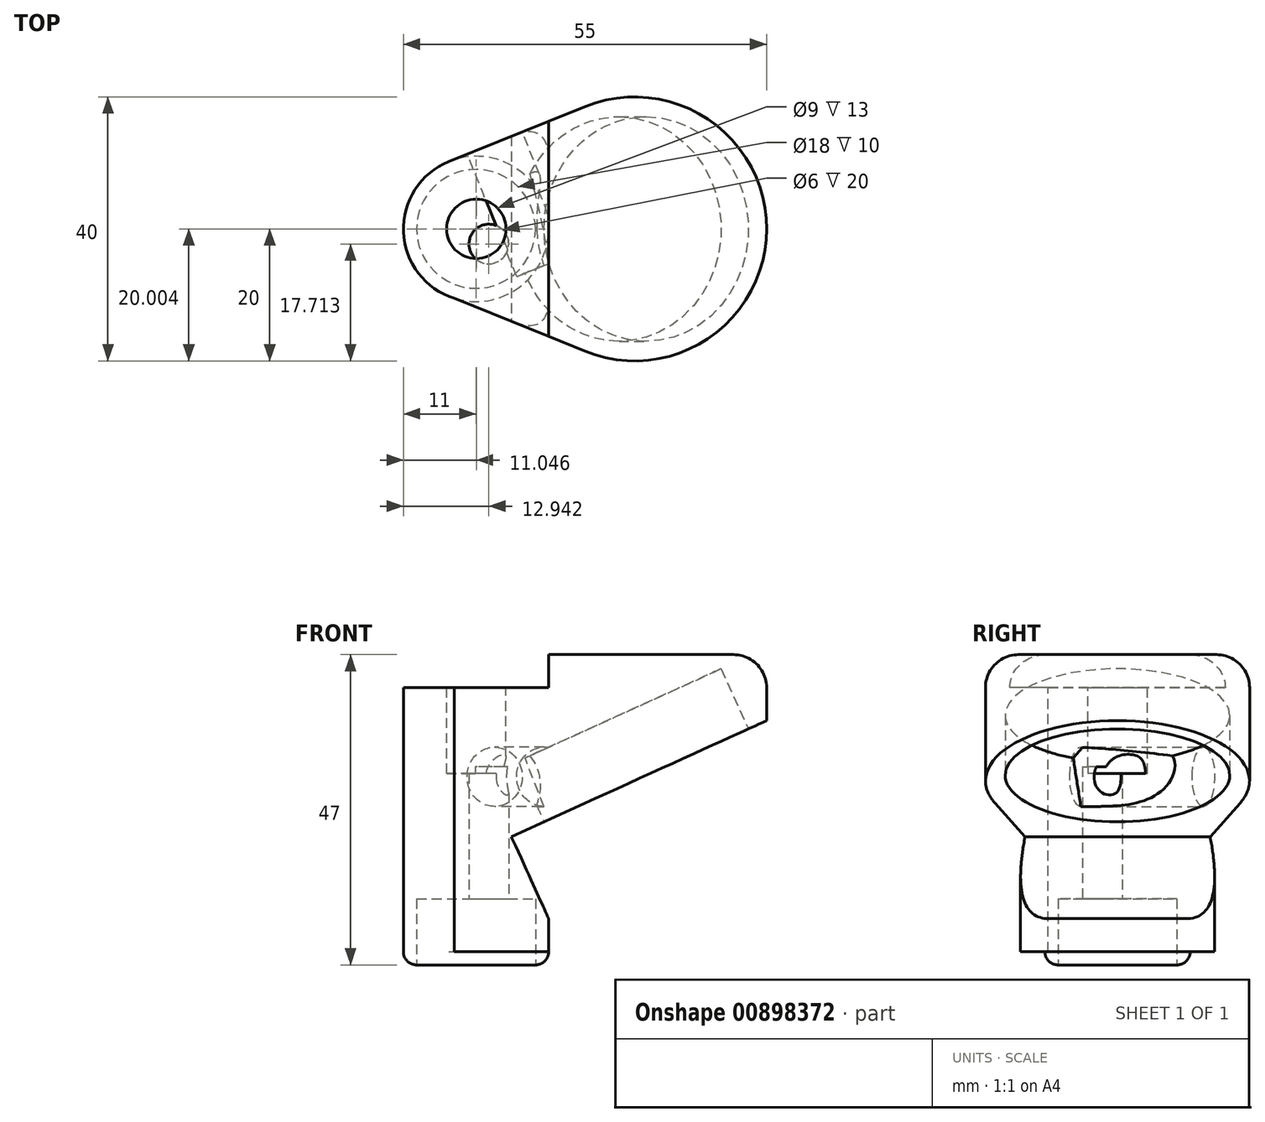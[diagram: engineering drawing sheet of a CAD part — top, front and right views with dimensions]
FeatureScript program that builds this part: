
annotation { "Feature Type Name" : "Feature", "Feature Type Description" : "" }
export const myFeature = defineFeature(function(context is Context, id is Id, definition is map)
    precondition{}
    {
        {
            var Q0;
            Q0=qCreatedBy(makeId("Top.planeOp"),FACE);
            var sketch = newSketch(context, id + "F0", { "sketchPlane" : qUnion([Q0])});
            skLineSegment(sketch, "E0.bottom", {"start": v(27.5, -20) * mm, "end": v(-27.5, -20) * mm});
            skLineSegment(sketch, "E0.top", {"start": v(27.5, 20) * mm, "end": v(-27.5, 20) * mm});
            skLineSegment(sketch, "E0.left", {"start": v(27.5, -20) * mm, "end": v(27.5, 20) * mm});
            skLineSegment(sketch, "E0.right", {"start": v(-27.5, -20) * mm, "end": v(-27.5, 20) * mm});
            skPoint(sketch, "E0.middle", {"position": v(0, 0) * mm});
            skSolve(sketch);
        }
        {
            var Q0;
            Q0=makeQuery(id+"F0.imprint","IMPRINT",FACE,{"disambiguationData":[TD([[makeQuery(id+"F0.imprint","IMPRINT",EDGE,{"derivedFrom":sQuery(id+"F0.wireOp",EDGE,"E0.bottom")}),-1.0]])]});
            extrude(context, id + "F1", {"entities" : qUnion([Q0]), "depth" : 45 * mm, "offsetDistance" : 25 * mm});
        }
        {
            var Q0;
            Q0=makeQuery(id+"F1.opExtrude","CAP_FACE",FACE,{"disambiguationData":[OSD([sQuery(id+"F0.wireOp",EDGE,"E0.bottom"),sQuery(id+"F0.wireOp",EDGE,"E0.top"),sQuery(id+"F0.wireOp",EDGE,"E0.left"),sQuery(id+"F0.wireOp",EDGE,"E0.right")])],"isStart":false});
            var sketch = newSketch(context, id + "F2", { "sketchPlane" : qUnion([Q0])});
            skPoint(sketch, "E1.first.point", {"position": v(27.5, 0) * mm});
            skLineSegment(sketch, "E2", {"start": v(6.08, -20) * mm, "end": v(27.5, -20) * mm});
            skLineSegment(sketch, "E3", {"start": v(27.5, 20) * mm, "end": v(6.08, 20) * mm});
            skCircle(sketch, "E4", {"center": v(-16.5, 0) * mm, "radius": 11 * mm});
            skPoint(sketch, "E4.centerSnap0", {"position": v(-16.5, 20) * mm});
            skLineSegment(sketch, "E5.left", {"start": v(27.5, 20) * mm, "end": v(27.5, -20) * mm});
            skCircle(sketch, "E6", {"center": v(7.5, 0) * mm, "radius": 20 * mm});
            skPoint(sketch, "E6.centerSnap0", {"position": v(7.5, 20) * mm});
            skLineSegment(sketch, "E7", {"start": v(-20.63, 10.2) * mm, "end": v(0, 18.54) * mm});
            skLineSegment(sketch, "E8", {"start": v(-19.77, -10.5) * mm, "end": v(0, -18.54) * mm});
            skSolve(sketch);
        }
        {
            var Q0;
            Q0=makeQuery(id+"F1.opExtrude","SWEPT_FACE",FACE,{"disambiguationData":[OSD([sQuery(id+"F0.wireOp",EDGE,"E0.bottom")])]});
            var sketch = newSketch(context, id + "F3", { "sketchPlane" : qUnion([Q0])});
            skLineSegment(sketch, "E9.bottom", {"start": v(27.5, 0) * mm, "end": v(-5.5, 0) * mm});
            skLineSegment(sketch, "E9.top", {"start": v(27.5, 5) * mm, "end": v(-5.5, 5) * mm});
            skLineSegment(sketch, "E9.left", {"start": v(27.5, 0) * mm, "end": v(27.5, 5) * mm});
            skLineSegment(sketch, "E9.right", {"start": v(-5.5, 0) * mm, "end": v(-5.5, 5) * mm});
            skLineSegment(sketch, "E10", {"start": v(27.5, 5) * mm, "end": v(27.5, 35) * mm});
            skLineSegment(sketch, "E11", {"start": v(27.5, 35) * mm, "end": v(-5.5, 20) * mm});
            skLineSegment(sketch, "E12", {"start": v(-5.5, 20) * mm, "end": v(-11.15, 17.43) * mm});
            skLineSegment(sketch, "E13", {"start": v(-11.15, 17.43) * mm, "end": v(-5.5, 5) * mm});
            skSolve(sketch);
        }
        {
            var Q0;
            Q0 = qSketchRegion(id + "F3", true);
            extrude(context, id + "F4", {"entities" : qUnion([Q0]), "operationType" : NewBodyOperationType.REMOVE, "endBound" : BoundingType.THROUGH_ALL, "oppositeDirection" : true, "depth" : 25 * mm, "offsetDistance" : 25 * mm});
        }
        {
            var Q0;
            Q0=makeQuery(id+"F1.opExtrude","CAP_FACE",FACE,{"disambiguationData":[OSD([sQuery(id+"F0.wireOp",EDGE,"E0.bottom"),sQuery(id+"F0.wireOp",EDGE,"E0.top"),sQuery(id+"F0.wireOp",EDGE,"E0.left"),sQuery(id+"F0.wireOp",EDGE,"E0.right")])],"isStart":true});
            var sketch = newSketch(context, id + "F5", { "sketchPlane" : qUnion([Q0])});
            skCircle(sketch, "E14", {"center": v(-16.5, 0) * mm, "radius": 11 * mm});
            skPoint(sketch, "E14.centerSnap0", {"position": v(-16.5, -20) * mm});
            skSolve(sketch);
        }
        {
            var Q0;
            {var subQ0=sQuery(id+"F5.wireOp",EDGE,"E14");var subQ1=makeQuery(id+"F5.imprint","INTERSECT",VERTEX,{"derivedFrom":[makeQuery(id+"F1.opExtrude","CAP_EDGE",EDGE,{"disambiguationData":[OSD([sQuery(id+"F0.wireOp",EDGE,"E0.right")])],"isStart":true}),subQ0]});Q0=makeQuery(id+"F5.imprint","IMPRINT",FACE,{"disambiguationData":[TD([[makeQuery(id+"F5.imprint","IMPRINT",EDGE,{"disambiguationData":[TD([[subQ1,1.0]])],"derivedFrom":subQ0}),1.0]])]});}
            extrude(context, id + "F6", {"entities" : qUnion([Q0]), "operationType" : NewBodyOperationType.ADD, "depth" : 2 * mm, "offsetDistance" : 25 * mm});
        }
        {
            var Q0;
            Q0=makeQuery(id+"F6.opExtrude","CAP_FACE",FACE,{"disambiguationData":[OSD([sQuery(id+"F5.wireOp",EDGE,"E14")])],"isStart":false});
            fillet(context, id + "F7", {"entities" : qUnion([Q0]), "radius" : 2 * mm, "tangentPropagation" : true, "allowEdgeOverflow" : false});
        }
        {
            var Q0;
            Q0=makeQuery(id+"F1.opExtrude","SWEPT_FACE",FACE,{"disambiguationData":[OSD([sQuery(id+"F0.wireOp",EDGE,"E0.bottom")])]});
            var sketch = newSketch(context, id + "F8", { "sketchPlane" : qUnion([Q0])});
            skLineSegment(sketch, "E15.bottom", {"start": v(-27.5, 45) * mm, "end": v(-5.5, 45) * mm});
            skLineSegment(sketch, "E15.top", {"start": v(-27.5, 40) * mm, "end": v(-5.5, 40) * mm});
            skLineSegment(sketch, "E15.left", {"start": v(-27.5, 45) * mm, "end": v(-27.5, 40) * mm});
            skLineSegment(sketch, "E15.right", {"start": v(-5.5, 45) * mm, "end": v(-5.5, 40) * mm});
            skSolve(sketch);
        }
        {
            var Q0;
            {var subQ4=sQuery(id+"F2.wireOp",EDGE,"E8");Q0=makeQuery(id+"F2.imprint","IMPRINT",FACE,{"disambiguationData":[TD([[makeQuery(id+"F2.imprint","IMPRINT",EDGE,{"derivedFrom":subQ4}),-1.0]])]});}
            var Q1;
            {var subQ4=sQuery(id+"F2.wireOp",EDGE,"E7");Q1=makeQuery(id+"F2.imprint","IMPRINT",FACE,{"disambiguationData":[TD([[makeQuery(id+"F2.imprint","IMPRINT",EDGE,{"derivedFrom":subQ4}),1.0]])]});}
            extrude(context, id + "F9", {"entities" : qUnion([Q0, Q1]), "operationType" : NewBodyOperationType.REMOVE, "endBound" : BoundingType.THROUGH_ALL, "oppositeDirection" : true, "depth" : 25 * mm, "offsetDistance" : 25 * mm});
        }
        {
            var Q0;
            Q0=makeQuery(id+"F8.imprint","IMPRINT",FACE,{"disambiguationData":[TD([[makeQuery(id+"F8.imprint","IMPRINT",EDGE,{"derivedFrom":sQuery(id+"F8.wireOp",EDGE,"E15.bottom")}),1.0]])]});
            extrude(context, id + "F10", {"entities" : qUnion([Q0]), "operationType" : NewBodyOperationType.REMOVE, "endBound" : BoundingType.THROUGH_ALL, "oppositeDirection" : true, "depth" : 25 * mm, "offsetDistance" : 25 * mm});
        }
        {
            var Q0;
            Q0=makeQuery(id+"F10.boolean.opBoolean","COPY",FACE,{"derivedFrom":makeQuery(id+"F10.opExtrude","SWEPT_FACE",FACE,{"disambiguationData":[OSD([sQuery(id+"F8.wireOp",EDGE,"E15.top")])]})});
            var sketch = newSketch(context, id + "F11", { "sketchPlane" : qUnion([Q0])});
            skCircle(sketch, "E16", {"center": v(-16.45, 0) * mm, "radius": 4.5 * mm});
            skSolve(sketch);
        }
        {
            var Q0;
            Q0=makeQuery(id+"F11.imprint","IMPRINT",FACE,{"disambiguationData":[TD([[makeQuery(id+"F11.imprint","IMPRINT",EDGE,{"derivedFrom":sQuery(id+"F11.wireOp",EDGE,"E16")}),1.0]])]});
            extrude(context, id + "F12", {"entities" : qUnion([Q0]), "operationType" : NewBodyOperationType.REMOVE, "oppositeDirection" : true, "depth" : 13 * mm, "offsetDistance" : 25 * mm});
        }
        {
            var Q0;
            Q0=makeQuery(id+"F4.boolean.opBoolean","COPY",FACE,{"derivedFrom":makeQuery(id+"F4.opExtrude","SWEPT_FACE",FACE,{"disambiguationData":[OSD([sQuery(id+"F3.wireOp",EDGE,"E11"),sQuery(id+"F3.wireOp",EDGE,"E12")])]})});
            var sketch = newSketch(context, id + "F13", { "sketchPlane" : qUnion([Q0])});
            skPoint(sketch, "E17.first.point", {"position": v(39.52, 0) * mm});
            skPoint(sketch, "E17.second.point", {"position": v(20.48, 20) * mm});
            skPoint(sketch, "E17.third.point", {"position": v(19.91, -20) * mm});
            skCircle(sketch, "E18", {"center": v(19.5, 0) * mm, "radius": 17 * mm});
            skSolve(sketch);
        }
        {
            var Q0;
            Q0=makeQuery(id+"F13.imprint","IMPRINT",FACE,{"disambiguationData":[TD([[makeQuery(id+"F13.imprint","IMPRINT",EDGE,{"derivedFrom":sQuery(id+"F13.wireOp",EDGE,"E18")}),1.0]])]});
            extrude(context, id + "F14", {"entities" : qUnion([Q0]), "operationType" : NewBodyOperationType.REMOVE, "oppositeDirection" : true, "depth" : 10 * mm, "offsetDistance" : 25 * mm});
        }
        {
            var Q0;
            Q0=makeQuery(id+"F6.opExtrude","CAP_FACE",FACE,{"disambiguationData":[OSD([sQuery(id+"F5.wireOp",EDGE,"E14")])],"isStart":false});
            extrude(context, id + "F15", {"entities" : qUnion([Q0]), "operationType" : NewBodyOperationType.REMOVE, "oppositeDirection" : true, "depth" : 10 * mm, "offsetDistance" : 25 * mm});
        }
        {
            var Q0;
            {var subQ0=sQuery(id+"F2.wireOp",EDGE,"E5.left");var subQ1=sQuery(id+"F2.wireOp",EDGE,"E2");var subQ2=makeQuery(id+"F2.imprint","INTERSECT",VERTEX,{"derivedFrom":[subQ1,subQ0]});Q0=makeQuery(id+"F2.imprint","IMPRINT",FACE,{"disambiguationData":[TD([[makeQuery(id+"F2.imprint","IMPRINT",EDGE,{"disambiguationData":[TD([[subQ2,-1.0]])],"derivedFrom":subQ1}),-1.0]])]});}
            extrude(context, id + "F16", {"entities" : qUnion([Q0]), "operationType" : NewBodyOperationType.REMOVE, "endBound" : BoundingType.THROUGH_ALL, "oppositeDirection" : true, "depth" : 25 * mm, "offsetDistance" : 25 * mm});
        }
        {
            var Q0;
            Q0=makeQuery(id+"F1.opExtrude","SWEPT_EDGE",EDGE,{"disambiguationData":[OSD([sQuery(id+"F0.wireOp",EDGE,"E0.top"),sQuery(id+"F0.wireOp",EDGE,"E0.left")])]});
            fillet(context, id + "F17", {"entities" : qUnion([Q0]), "radius" : 20 * mm, "tangentPropagation" : true, "allowEdgeOverflow" : false});
        }
        {
            var Q0;
            Q0=makeQuery(id+"F9.boolean.opBoolean","INTERSECT",EDGE,{"derivedFrom":[makeQuery(id+"F4.boolean.opBoolean","COPY",FACE,{"derivedFrom":makeQuery(id+"F4.opExtrude","SWEPT_FACE",FACE,{"disambiguationData":[OSD([sQuery(id+"F3.wireOp",EDGE,"E9.right")])]})}),makeQuery(id+"F9.opExtrude","SWEPT_FACE",FACE,{"disambiguationData":[OSD([sQuery(id+"F2.wireOp",EDGE,"E7")])]})]});
            fillet(context, id + "F18", {"entities" : qUnion([Q0]), "radius" : 4 * mm, "tangentPropagation" : true, "rho" : 0.5, "crossSection" : FilletCrossSection.CONIC, "allowEdgeOverflow" : false});
        }
        {
            var Q0;
            Q0=makeQuery(id+"F9.boolean.opBoolean","INTERSECT",EDGE,{"derivedFrom":[makeQuery(id+"F4.boolean.opBoolean","COPY",FACE,{"derivedFrom":makeQuery(id+"F4.opExtrude","SWEPT_FACE",FACE,{"disambiguationData":[OSD([sQuery(id+"F3.wireOp",EDGE,"E9.right")])]})}),makeQuery(id+"F9.opExtrude","SWEPT_FACE",FACE,{"disambiguationData":[OSD([sQuery(id+"F2.wireOp",EDGE,"E8")])]})]});
            fillet(context, id + "F19", {"entities" : qUnion([Q0]), "radius" : 4 * mm, "tangentPropagation" : true, "rho" : 0.5, "crossSection" : FilletCrossSection.CONIC, "allowEdgeOverflow" : false});
        }
        {
            var Q0;
            {var subQ0=sQuery(id+"F0.wireOp",EDGE,"E0.left");var subQ1=sQuery(id+"F0.wireOp",EDGE,"E0.top");var subQ2=sQuery(id+"F2.wireOp",EDGE,"E6");var subQ3=makeQuery(id+"F2.imprint","IMPRINT",VERTEX,{"derivedFrom":subQ2});Q0=makeQuery(id+"F19.opFillet","MERGE",EDGE,{"derivedFrom":[makeQuery(id+"F16.boolean.opBoolean","MERGE",EDGE,{"derivedFrom":[makeQuery(id+"F9.boolean.opBoolean","COPY",EDGE,{"derivedFrom":makeQuery(id+"F9.opExtrude","CAP_EDGE",EDGE,{"disambiguationData":[OSD([subQ2]),TDD([makeQuery(id+"F2.imprint","IMPRINT",EDGE,{"disambiguationData":[TD([[subQ3,1.0]])],"derivedFrom":subQ2}),makeQuery(id+"F2.imprint","IMPRINT",EDGE,{"disambiguationData":[TD([[subQ3,-1.0]])],"derivedFrom":subQ2})])],"isStart":true})})],"fromTools":[makeQuery(id+"F16.opExtrude","CAP_EDGE",EDGE,{"disambiguationData":[OSD([subQ2])],"isStart":true})]}),makeQuery(id+"F18.opFillet","MERGE",EDGE,{"derivedFrom":[makeQuery(id+"F9.boolean.opBoolean","COPY",EDGE,{"derivedFrom":makeQuery(id+"F9.opExtrude","CAP_EDGE",EDGE,{"disambiguationData":[OSD([subQ2]),TDD([makeQuery(id+"F2.imprint","IMPRINT",EDGE,{"disambiguationData":[TD([[makeQuery(id+"F2.imprint","INTERSECT",VERTEX,{"derivedFrom":[subQ2,sQuery(id+"F2.wireOp",EDGE,"E7")]}),1.0]])],"derivedFrom":subQ2})])],"isStart":true})}),makeQuery(id+"F17.opFillet","BLEND_EDGE",EDGE,{"blendedFrom":[makeQuery(id+"F1.opExtrude","SWEPT_EDGE",EDGE,{"disambiguationData":[OSD([subQ1,subQ0])]}),makeQuery(id+"F1.opExtrude","CAP_FACE",FACE,{"disambiguationData":[OSD([sQuery(id+"F0.wireOp",EDGE,"E0.bottom"),subQ1,subQ0,sQuery(id+"F0.wireOp",EDGE,"E0.right")])],"isStart":false})],"blendedInto":[makeQuery(id+"F1.opExtrude","CAP_FACE",FACE,{"disambiguationData":[OSD([sQuery(id+"F0.wireOp",EDGE,"E0.bottom"),subQ1,subQ0,sQuery(id+"F0.wireOp",EDGE,"E0.right")])],"isStart":false})]})]})]});}
            fillet(context, id + "F20", {"entities" : qUnion([Q0]), "radius" : 5 * mm, "tangentPropagation" : true, "allowEdgeOverflow" : false});
        }
        {
            var Q0;
            Q0=makeQuery(id+"F9.boolean.opBoolean","COPY",FACE,{"derivedFrom":makeQuery(id+"F9.opExtrude","SWEPT_FACE",FACE,{"disambiguationData":[OSD([sQuery(id+"F2.wireOp",EDGE,"E7")])]})});
            var sketch = newSketch(context, id + "F21", { "sketchPlane" : qUnion([Q0])});
            skCircle(sketch, "E19", {"center": v(7.8, 26.5) * mm, "radius": 4.5 * mm});
            skSolve(sketch);
        }
        {
            var Q0;
            Q0=makeQuery(id+"F21.imprint","IMPRINT",FACE,{"disambiguationData":[TD([[makeQuery(id+"F21.imprint","IMPRINT",EDGE,{"derivedFrom":sQuery(id+"F21.wireOp",EDGE,"E19")}),1.0]])]});
            extrude(context, id + "F22", {"entities" : qUnion([Q0]), "operationType" : NewBodyOperationType.REMOVE, "oppositeDirection" : true, "depth" : 20 * mm, "offsetDistance" : 25 * mm});
        }
        {
            var Q0;
            Q0=makeQuery(id+"F15.boolean.opBoolean","COPY",FACE,{"derivedFrom":makeQuery(id+"F15.opExtrude","CAP_FACE",FACE,{"disambiguationData":[OSD([sQuery(id+"F5.wireOp",EDGE,"E14")])],"isStart":false})});
            var sketch = newSketch(context, id + "F23", { "sketchPlane" : qUnion([Q0])});
            skCircle(sketch, "E20", {"center": v(-14.56, 2.29) * mm, "radius": 3 * mm});
            skSolve(sketch);
        }
        {
            var Q0;
            Q0=makeQuery(id+"F23.imprint","IMPRINT",FACE,{"disambiguationData":[TD([[makeQuery(id+"F23.imprint","IMPRINT",EDGE,{"derivedFrom":sQuery(id+"F23.wireOp",EDGE,"E20")}),1.0]])]});
            var Q1;
            Q1=sQuery(id+"F23.wireOp",EDGE,"E20");
            extrude(context, id + "F24", {"entities" : qUnion([Q0]), "operationType" : NewBodyOperationType.REMOVE, "surfaceEntities" : qUnion([Q1]), "oppositeDirection" : true, "depth" : 20 * mm, "offsetDistance" : 25 * mm});
        }
    });
